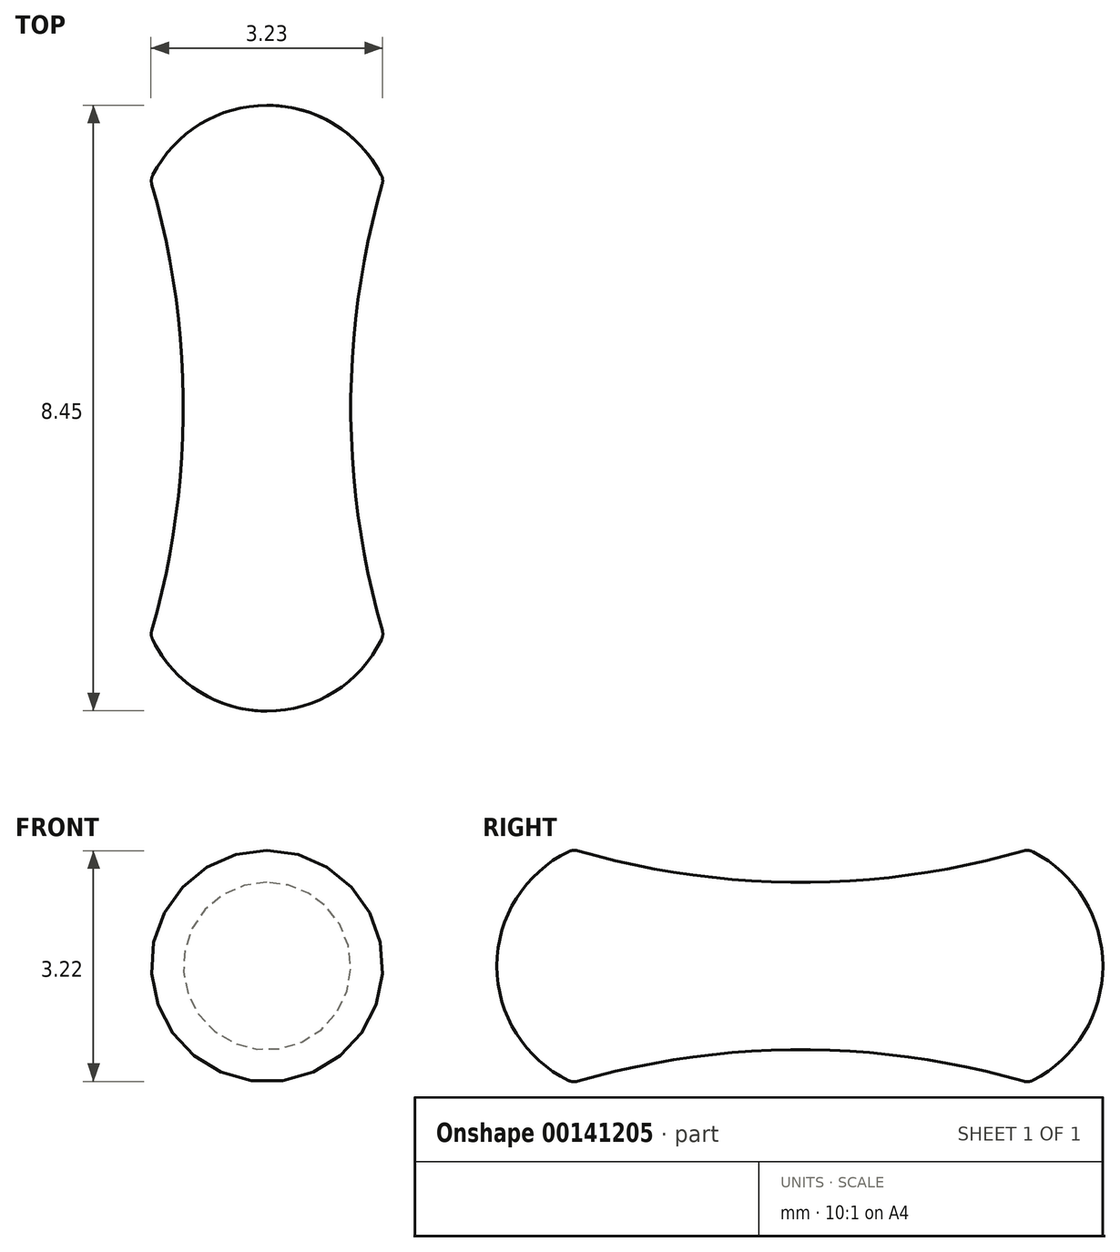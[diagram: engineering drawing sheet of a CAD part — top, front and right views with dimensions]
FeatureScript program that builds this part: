
annotation { "Feature Type Name" : "Feature", "Feature Type Description" : "" }
export const myFeature = defineFeature(function(context is Context, id is Id, definition is map)
    precondition{}
    {
        {
            var Q0;
            Q0=qCreatedBy(makeId("Top.planeOp"),FACE);
            var sketch = newSketch(context, id + "F0", { "sketchPlane" : qUnion([Q0])});
            skArc(sketch, "E0", {"start": v(-5.73, 7.39) * mm, "mid": v(-6.66, 7.13) * mm, "end": v(-7.32, 6.42) * mm});
            skArc(sketch, "E1", {"start": v(-7.33, -0.06) * mm, "mid": v(-6.67, -0.8) * mm, "end": v(-5.73, -1.06) * mm});
            skArc(sketch, "E2", {"start": v(-7.34, 0.06) * mm, "mid": v(-6.9, 3.17) * mm, "end": v(-7.34, 6.28) * mm});
            skLineSegment(sketch, "E3", {"start": v(-5.73, 7.39) * mm, "end": v(-5.73, -1.06) * mm});
            skPoint(sketch, "E4.end.orphan", {"position": v(-4.1, 0) * mm});
            skPoint(sketch, "E5.visualSharp", {"position": v(-7.36, 0) * mm});
            skArc(sketch, "E5.filletArc", {"start": v(-7.34, 0.06) * mm, "mid": v(-7.34, 0) * mm, "end": v(-7.33, -0.06) * mm});
            skPoint(sketch, "E6.visualSharp", {"position": v(-7.36, 6.35) * mm});
            skArc(sketch, "E6.filletArc", {"start": v(-7.32, 6.42) * mm, "mid": v(-7.34, 6.35) * mm, "end": v(-7.34, 6.28) * mm});
            skSolve(sketch);
        }
        {
            var Q0;
            Q0=makeQuery(id+"F0.imprint","IMPRINT",FACE,{"disambiguationData":[TD([[makeQuery(id+"F0.imprint","IMPRINT",EDGE,{"derivedFrom":sQuery(id+"F0.wireOp",EDGE,"E0")}),1.0]])]});
            var Q1;
            Q1=sQuery(id+"F0.wireOp",EDGE,"E3");
            revolve(context, id + "F1", {"entities" : qUnion([Q0]), "axis" : qUnion([Q1]), "revolveType" : RevolveType.FULL});
        }
    });
